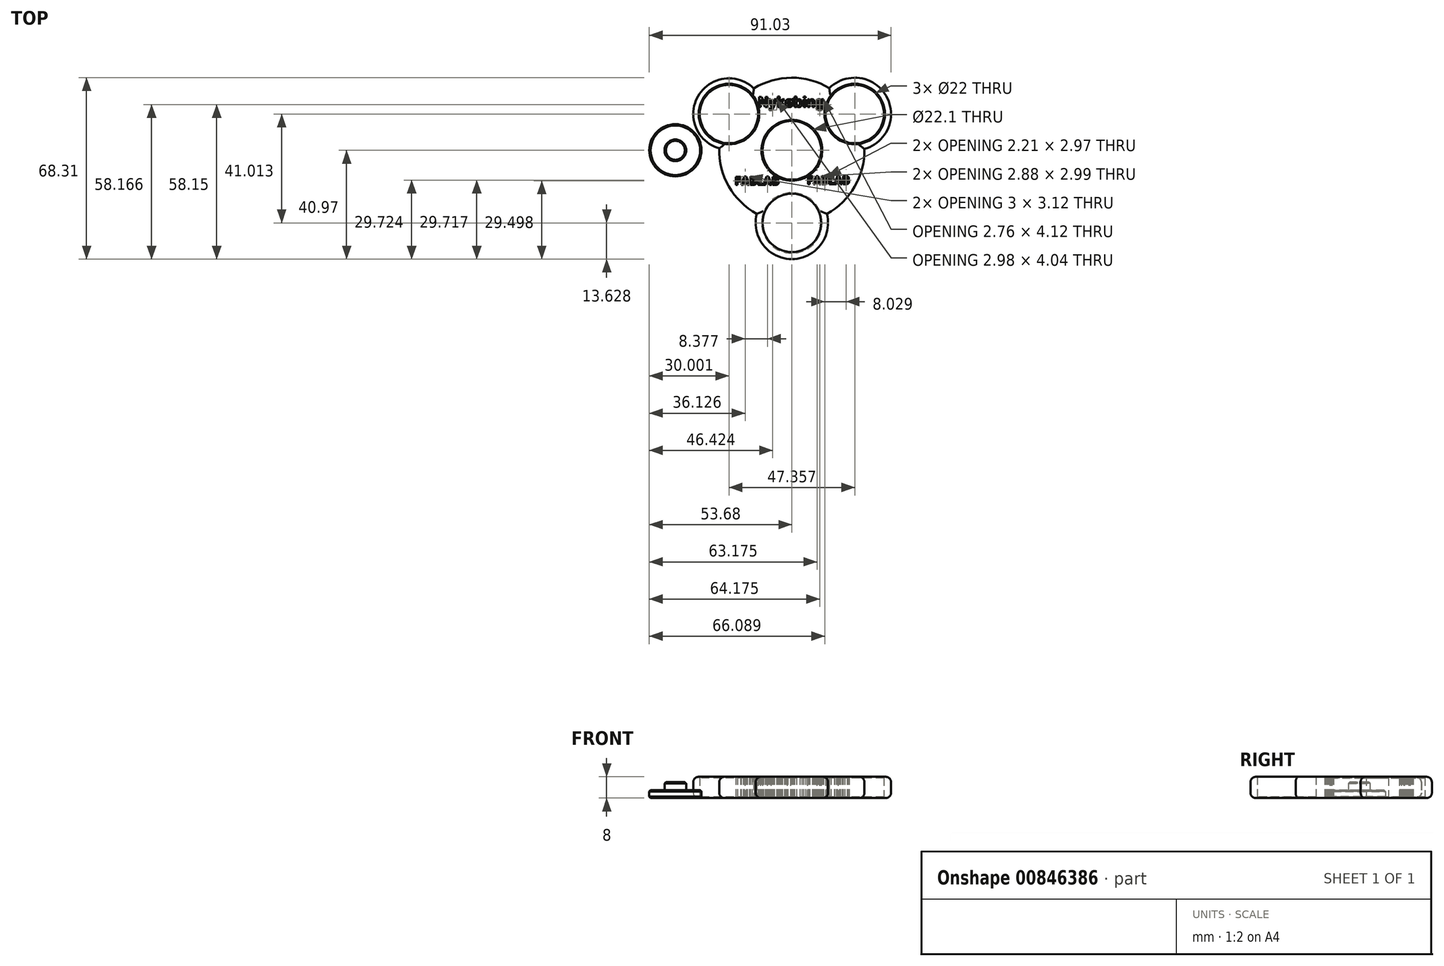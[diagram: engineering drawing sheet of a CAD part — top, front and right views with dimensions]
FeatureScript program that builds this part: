
annotation { "Feature Type Name" : "Feature", "Feature Type Description" : "" }
export const myFeature = defineFeature(function(context is Context, id is Id, definition is map)
    precondition{}
    {
        {
            var Q0;
            Q0=qCreatedBy(makeId("Top.planeOp"),FACE);
            var sketch = newSketch(context, id + "F0", { "sketchPlane" : qUnion([Q0])});
            skCircle(sketch, "E0", {"center": v(0, 0) * mm, "radius": 11.05 * mm});
            skCircle(sketch, "E1", {"center": v(0, -27.34) * mm, "radius": 11 * mm});
            skArc(sketch, "E2", {"start": v(-27.33, 0.74) * mm, "mid": v(-23.73, -13.58) * mm, "end": v(-13.2, -23.94) * mm});
            skCircle(sketch, "E3", {"center": v(-23.68, 13.67) * mm, "radius": 11 * mm});
            skCircle(sketch, "E4", {"center": v(23.68, 13.67) * mm, "radius": 11 * mm});
            skArc(sketch, "E5", {"start": v(27.34, 0.5) * mm, "mid": v(35.51, 20.5) * mm, "end": v(14.1, 23.42) * mm});
            skArc(sketch, "E6", {"start": v(-13.2, -23.94) * mm, "mid": v(0, -40.97) * mm, "end": v(13.2, -23.94) * mm});
            skArc(sketch, "E7.trimOffspring", {"start": v(13.2, -23.94) * mm, "mid": v(23.67, -13.69) * mm, "end": v(27.34, 0.5) * mm});
            skArc(sketch, "E8.trimOffspring", {"start": v(14.1, 23.42) * mm, "mid": v(-0.12, 27.34) * mm, "end": v(-14.3, 23.3) * mm});
            skArc(sketch, "E9", {"start": v(-14.3, 23.3) * mm, "mid": v(-35.31, 20.39) * mm, "end": v(-27.33, 0.74) * mm});
            skLineSegment(sketch, "E10", {"start": v(-14.3, 23.3) * mm, "end": v(-5.78, 9.42) * mm});
            skLineSegment(sketch, "E11", {"start": v(5.7, 9.47) * mm, "end": v(14.1, 23.42) * mm});
            skLineSegment(sketch, "E12", {"start": v(11.05, 0.2) * mm, "end": v(27.34, 0.5) * mm});
            skLineSegment(sketch, "E13", {"start": v(-11.05, 0.3) * mm, "end": v(-27.33, 0.74) * mm});
            skLineSegment(sketch, "E14", {"start": v(-5.33, -9.68) * mm, "end": v(-13.2, -23.94) * mm});
            skLineSegment(sketch, "E15", {"start": v(5.33, -9.68) * mm, "end": v(13.2, -23.94) * mm});
            skPoint(sketch, "E16", {"position": v(-47, 0) * mm});
            skPoint(sketch, "E17", {"position": v(47.85, 0) * mm});
            skCircle(sketch, "E18", {"center": v(-47, 0) * mm, "radius": 9.55 * mm});
            skCircle(sketch, "E19", {"center": v(47.85, 0) * mm, "radius": 9.73 * mm});
            skCircle(sketch, "E20", {"center": v(-47, 0) * mm, "radius": 4 * mm});
            skCircle(sketch, "E21", {"center": v(47.85, 0) * mm, "radius": 4 * mm});
            skSolve(sketch);
        }
        {
            var Q0;
            Q0=makeQuery(id+"F0.imprint","IMPRINT",FACE,{"disambiguationData":[TD([[makeQuery(id+"F0.imprint","IMPRINT",EDGE,{"derivedFrom":sQuery(id+"F0.wireOp",EDGE,"E3")}),-1.0]])]});
            var Q1;
            Q1=makeQuery(id+"F0.imprint","IMPRINT",FACE,{"disambiguationData":[TD([[makeQuery(id+"F0.imprint","IMPRINT",EDGE,{"derivedFrom":sQuery(id+"F0.wireOp",EDGE,"E4")}),-1.0]])]});
            var Q2;
            Q2=makeQuery(id+"F0.imprint","IMPRINT",FACE,{"disambiguationData":[TD([[makeQuery(id+"F0.imprint","IMPRINT",EDGE,{"derivedFrom":sQuery(id+"F0.wireOp",EDGE,"E1")}),-1.0]])]});
            var Q3;
            Q3=makeQuery(id+"F0.imprint","IMPRINT",FACE,{"disambiguationData":[TD([[makeQuery(id+"F0.imprint","IMPRINT",EDGE,{"derivedFrom":sQuery(id+"F0.wireOp",EDGE,"E2")}),1.0]])]});
            var Q4;
            Q4=makeQuery(id+"F0.imprint","IMPRINT",FACE,{"disambiguationData":[TD([[makeQuery(id+"F0.imprint","IMPRINT",EDGE,{"derivedFrom":sQuery(id+"F0.wireOp",EDGE,"E8.trimOffspring")}),1.0]])]});
            var Q5;
            Q5=makeQuery(id+"F0.imprint","IMPRINT",FACE,{"disambiguationData":[TD([[makeQuery(id+"F0.imprint","IMPRINT",EDGE,{"derivedFrom":sQuery(id+"F0.wireOp",EDGE,"E7.trimOffspring")}),1.0]])]});
            extrude(context, id + "F1", {"entities" : qUnion([Q0, Q1, Q2, Q3, Q4, Q5]), "depth" : 8 * mm, "offsetDistance" : 25 * mm});
        }
        {
            var Q0;
            Q0=makeQuery(id+"F1.opExtrude","CAP_EDGE",EDGE,{"disambiguationData":[OSD([sQuery(id+"F0.wireOp",EDGE,"E8.trimOffspring")])],"isStart":false});
            var Q1;
            Q1=makeQuery(id+"F1.opExtrude","CAP_EDGE",EDGE,{"disambiguationData":[OSD([sQuery(id+"F0.wireOp",EDGE,"E9")])],"isStart":false});
            var Q2;
            Q2=makeQuery(id+"F1.opExtrude","CAP_EDGE",EDGE,{"disambiguationData":[OSD([sQuery(id+"F0.wireOp",EDGE,"E2")])],"isStart":false});
            var Q3;
            Q3=makeQuery(id+"F1.opExtrude","CAP_EDGE",EDGE,{"disambiguationData":[OSD([sQuery(id+"F0.wireOp",EDGE,"E6")])],"isStart":false});
            var Q4;
            Q4=makeQuery(id+"F1.opExtrude","CAP_EDGE",EDGE,{"disambiguationData":[OSD([sQuery(id+"F0.wireOp",EDGE,"E7.trimOffspring")])],"isStart":false});
            var Q5;
            Q5=makeQuery(id+"F1.opExtrude","CAP_EDGE",EDGE,{"disambiguationData":[OSD([sQuery(id+"F0.wireOp",EDGE,"E5")])],"isStart":false});
            var Q6;
            Q6=makeQuery(id+"F1.opExtrude","CAP_EDGE",EDGE,{"disambiguationData":[OSD([sQuery(id+"F0.wireOp",EDGE,"E7.trimOffspring")])],"isStart":true});
            var Q7;
            Q7=makeQuery(id+"F1.opExtrude","CAP_EDGE",EDGE,{"disambiguationData":[OSD([sQuery(id+"F0.wireOp",EDGE,"E6")])],"isStart":true});
            var Q8;
            Q8=makeQuery(id+"F1.opExtrude","CAP_EDGE",EDGE,{"disambiguationData":[OSD([sQuery(id+"F0.wireOp",EDGE,"E2")])],"isStart":true});
            var Q9;
            Q9=makeQuery(id+"F1.opExtrude","CAP_EDGE",EDGE,{"disambiguationData":[OSD([sQuery(id+"F0.wireOp",EDGE,"E9")])],"isStart":true});
            var Q10;
            Q10=makeQuery(id+"F1.opExtrude","CAP_EDGE",EDGE,{"disambiguationData":[OSD([sQuery(id+"F0.wireOp",EDGE,"E8.trimOffspring")])],"isStart":true});
            var Q11;
            Q11=makeQuery(id+"F1.opExtrude","CAP_EDGE",EDGE,{"disambiguationData":[OSD([sQuery(id+"F0.wireOp",EDGE,"E5")])],"isStart":true});
            fillet(context, id + "F2", {"entities" : qUnion([Q0, Q1, Q2, Q3, Q4, Q5, Q6, Q7, Q8, Q9, Q10, Q11]), "radius" : 2 * mm, "tangentPropagation" : true, "allowEdgeOverflow" : false});
        }
        {
            var Q0;
            Q0=makeQuery(id+"F1.opExtrude","CAP_EDGE",EDGE,{"disambiguationData":[OSD([sQuery(id+"F0.wireOp",EDGE,"E0")])],"isStart":false});
            var Q1;
            Q1=makeQuery(id+"F1.opExtrude","CAP_EDGE",EDGE,{"disambiguationData":[OSD([sQuery(id+"F0.wireOp",EDGE,"E3")])],"isStart":false});
            var Q2;
            Q2=makeQuery(id+"F1.opExtrude","CAP_EDGE",EDGE,{"disambiguationData":[OSD([sQuery(id+"F0.wireOp",EDGE,"E4")])],"isStart":false});
            var Q3;
            Q3=makeQuery(id+"F1.opExtrude","CAP_EDGE",EDGE,{"disambiguationData":[OSD([sQuery(id+"F0.wireOp",EDGE,"E1")])],"isStart":true});
            var Q4;
            Q4=makeQuery(id+"F1.opExtrude","CAP_EDGE",EDGE,{"disambiguationData":[OSD([sQuery(id+"F0.wireOp",EDGE,"E0")])],"isStart":true});
            var Q5;
            Q5=makeQuery(id+"F1.opExtrude","CAP_EDGE",EDGE,{"disambiguationData":[OSD([sQuery(id+"F0.wireOp",EDGE,"E3")])],"isStart":true});
            var Q6;
            Q6=makeQuery(id+"F1.opExtrude","CAP_EDGE",EDGE,{"disambiguationData":[OSD([sQuery(id+"F0.wireOp",EDGE,"E4")])],"isStart":true});
            chamfer(context, id + "F3", {"entities" : qUnion([Q0, Q1, Q2, Q3, Q4, Q5, Q6]), "width" : 0.4 * mm, "tangentPropagation" : true});
        }
        {
            var Q0;
            Q0=qCreatedBy(makeId("Top.planeOp"),FACE);
            var sketch = newSketch(context, id + "F4", { "sketchPlane" : qUnion([Q0])});
            skPoint(sketch, "E22", {"position": v(-43.86, 0) * mm});
            skPoint(sketch, "E23", {"position": v(44.15, 0) * mm});
            skCircle(sketch, "E24", {"center": v(-43.86, 0) * mm, "radius": 9.92 * mm});
            skCircle(sketch, "E25", {"center": v(-43.86, 0) * mm, "radius": 4.08 * mm});
            skSolve(sketch);
        }
        {
            var Q0;
            Q0=makeQuery(id+"F4.imprint","IMPRINT",FACE,{"disambiguationData":[TD([[makeQuery(id+"F4.imprint","IMPRINT",EDGE,{"derivedFrom":sQuery(id+"F4.wireOp",EDGE,"E25")}),1.0]])]});
            extrude(context, id + "F5", {"entities" : qUnion([Q0]), "depth" : 6 * mm, "offsetDistance" : 25 * mm});
        }
        {
            var Q0;
            Q0=qCreatedBy(makeId("Top.planeOp"),FACE);
            var sketch = newSketch(context, id + "F6", { "sketchPlane" : qUnion([Q0])});
            skCircle(sketch, "E26", {"center": v(-43.86, 0) * mm, "radius": 9.82 * mm});
            skSolve(sketch);
        }
        {
            var Q0;
            Q0=makeQuery(id+"F6.imprint","IMPRINT",FACE,{"disambiguationData":[TD([[makeQuery(id+"F6.imprint","IMPRINT",EDGE,{"derivedFrom":sQuery(id+"F6.wireOp",EDGE,"E26")}),1.0]])]});
            extrude(context, id + "F7", {"entities" : qUnion([Q0]), "operationType" : NewBodyOperationType.ADD, "depth" : 3 * mm, "offsetDistance" : 25 * mm});
        }
        {
            var Q0;
            Q0=makeQuery(id+"F5.opExtrude","CAP_EDGE",EDGE,{"disambiguationData":[OSD([sQuery(id+"F4.wireOp",EDGE,"E25")])],"isStart":false});
            chamfer(context, id + "F8", {"entities" : qUnion([Q0]), "width" : 0.5 * mm, "tangentPropagation" : true});
        }
        {
            var Q0;
            Q0=makeQuery(id+"F7.opExtrude","CAP_EDGE",EDGE,{"disambiguationData":[OSD([sQuery(id+"F6.wireOp",EDGE,"E26")])],"isStart":false});
            var Q1;
            Q1=makeQuery(id+"F7.opExtrude","CAP_EDGE",EDGE,{"disambiguationData":[OSD([sQuery(id+"F6.wireOp",EDGE,"E26")])],"isStart":true});
            chamfer(context, id + "F9", {"entities" : qUnion([Q0, Q1]), "width" : 0.5 * mm, "tangentPropagation" : true});
        }
        {
            var Q0;
            Q0=qCreatedBy(makeId("Top.planeOp"),FACE);
            var sketch = newSketch(context, id + "F10", { "sketchPlane" : qUnion([Q0])});
            skText(sketch, "E27", { "text": "Nykøbing", "fontName": "Arimo-Bold.ttf"});
            const initialGuessF10  = {"E27": [-0.01275, 0.0163, 1, 0, 0.00395]};
            skSetInitialGuess(sketch, initialGuessF10);
            skSolve(sketch);
        }
        {
            var Q0;
            Q0=qSketchRegion(id+"FFkPs9eNDu4pnzR_2",true);
            var Q1;
            Q1=qSketchRegion(id+"F10",true);
            extrude(context, id + "F11", {"entities" : qUnion([Q0, Q1]), "operationType" : NewBodyOperationType.REMOVE, "depth" : 10 * mm, "offsetDistance" : 25 * mm});
        }
        {
            var Q0;
            Q0=qCreatedBy(makeId("Top.planeOp"),FACE);
            var sketch = newSketch(context, id + "F12", { "sketchPlane" : qUnion([Q0])});
            skText(sketch, "E28", { "text": "FABLAB", "fontName": "OpenSans-Bold.ttf"});
            const initialGuessF12  = {"E28": [-0.02144, -0.01303, 1, 0, 0.00313]};
            skSetInitialGuess(sketch, initialGuessF12);
            skSolve(sketch);
        }
        {
            var Q0;
            Q0=qCreatedBy(makeId("Top.planeOp"),FACE);
            var sketch = newSketch(context, id + "F13", { "sketchPlane" : qUnion([Q0])});
            skText(sketch, "E29", { "text": "FABLAB", "fontName": "OpenSans-Bold.ttf"});
            const initialGuessF13  = {"E29": [0.00577, -0.01274, 1, 0, 0.003]};
            skSetInitialGuess(sketch, initialGuessF13);
            skSolve(sketch);
        }
        {
            var Q0;
            Q0=qSketchRegion(id+"F12",true);
            var Q1;
            Q1=qSketchRegion(id+"F13",true);
            extrude(context, id + "F14", {"entities" : qUnion([Q0, Q1]), "operationType" : NewBodyOperationType.REMOVE, "depth" : 10 * mm, "offsetDistance" : 25 * mm});
        }
    });
